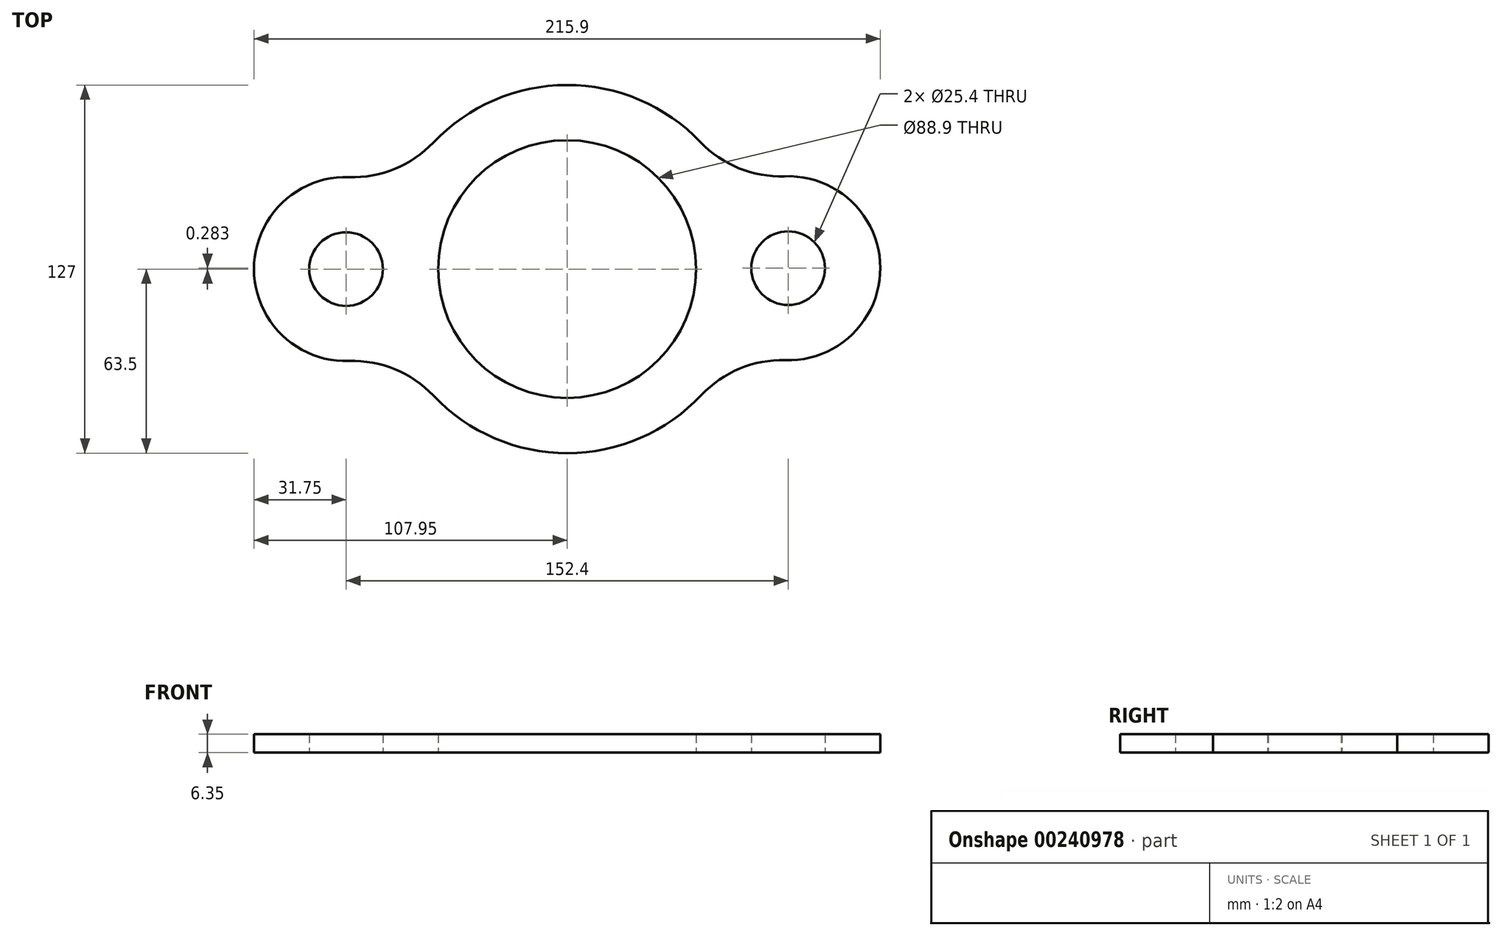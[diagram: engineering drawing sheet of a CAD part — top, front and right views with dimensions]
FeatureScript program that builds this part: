
annotation { "Feature Type Name" : "Feature", "Feature Type Description" : "" }
export const myFeature = defineFeature(function(context is Context, id is Id, definition is map)
    precondition{}
    {
        {
            var Q0;
            Q0=qCreatedBy(makeId("Top.planeOp"),FACE);
            var sketch = newSketch(context, id + "F0", { "sketchPlane" : qUnion([Q0])});
            skCircle(sketch, "E0", {"center": v(0, 0) * mm, "radius": 44.45 * mm});
            skArc(sketch, "E1", {"start": v(-46.14, -43.63) * mm, "mid": v(0.12, -63.5) * mm, "end": v(46.3, -43.46) * mm});
            skCircle(sketch, "E2", {"center": v(-76.2, 0) * mm, "radius": 12.7 * mm});
            skCircle(sketch, "E3", {"center": v(76.2, 0.28) * mm, "radius": 12.7 * mm});
            skArc(sketch, "E4", {"start": v(-75.12, 31.73) * mm, "mid": v(-107.95, 0) * mm, "end": v(-75.12, -31.73) * mm});
            skArc(sketch, "E5", {"start": v(75.24, -31.45) * mm, "mid": v(107.95, 0.4) * mm, "end": v(75, 32.01) * mm});
            skArc(sketch, "E6.trimOffspring", {"start": v(45.97, 43.8) * mm, "mid": v(-0.12, 63.5) * mm, "end": v(-46.14, 43.63) * mm});
            skPoint(sketch, "E7.visualSharp", {"position": v(-57.94, 25.98) * mm});
            skArc(sketch, "E7.filletArc", {"start": v(-75.12, 31.73) * mm, "mid": v(-59.35, 34.56) * mm, "end": v(-46.14, 43.63) * mm});
            skPoint(sketch, "E8.visualSharp", {"position": v(57.85, 26.2) * mm});
            skArc(sketch, "E8.filletArc", {"start": v(45.97, 43.8) * mm, "mid": v(59.22, 34.79) * mm, "end": v(75, 32.01) * mm});
            skPoint(sketch, "E9.visualSharp", {"position": v(58.04, -25.76) * mm});
            skArc(sketch, "E9.filletArc", {"start": v(75.24, -31.45) * mm, "mid": v(59.48, -34.34) * mm, "end": v(46.3, -43.46) * mm});
            skPoint(sketch, "E10.visualSharp", {"position": v(-57.94, -25.98) * mm});
            skArc(sketch, "E10.filletArc", {"start": v(-46.14, -43.63) * mm, "mid": v(-59.35, -34.56) * mm, "end": v(-75.12, -31.73) * mm});
            skSolve(sketch);
        }
        {
            var Q0;
            Q0=makeQuery(id+"F0.imprint","IMPRINT",FACE,{"disambiguationData":[TD([[makeQuery(id+"F0.imprint","IMPRINT",EDGE,{"derivedFrom":sQuery(id+"F0.wireOp",EDGE,"E0")}),-1.0]])]});
            extrude(context, id + "F1", {"entities" : qUnion([Q0]), "depth" : 6.35 * mm});
        }
    });
